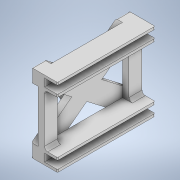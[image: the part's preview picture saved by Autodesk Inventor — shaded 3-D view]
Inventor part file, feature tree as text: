
AUTODESK INVENTOR PART (.ipt)
format: ipt  version: 2021 (Build 250183000, 183)  size: 252,928 bytes
history: native  units: in
note: dims shown in document units (in); Inventor stores cm internally (conversion verified against a paired STEP export)
features: extrude x4, fillet x4, sketch x4, plane x3
ambient origin geometry x8: Origin, YZ Plane, XZ Plane, XY Plane, X Axis, Y Axis, Z Axis, Center Point
bodies: Solid1 (feature_tree)
feature tree (15):
  extrude  "Extrusion1"  Depth=0.0394in TaperAngle=0.0deg
  plane  "Work Plane1"
  extrude  "Extrusion2"  Depth=0.5906in
  plane  "Work Plane2"
  extrude  "Extrusion3"  Depth=0.0787in
  plane  "Work Plane3"
  extrude  "Extrusion4"  Depth=0.0787in
  fillet  "Fillet1"  Radius=0.0787in
  fillet  "Fillet2"  Radius=0.0787in
  fillet  "Fillet3"  Radius=0.0787in
  fillet  "Fillet4"  Radius=0.0787in
  sketch  "Sketch1"  dims[d0=0.1969in d1=0.0394in d2=0.0in]
  sketch  "Sketch2"  dims[d3=0.0in d4=0.5906in]
  sketch  "Sketch3"  dims[d5=0.4724in d6=0.0787in]
  sketch  "Sketch4"  dims[d7=0.0787in d8=0.0787in d9=0.0787in d10=0.0787in d11=0.0787in d12=0.0787in d13=0.0787in d14=0.0394in d15=0.0in d16=0.0in d17=0.5906in d18=0.0394in d19=0.0in d20=0.0in d21=0.0157in d22=0.0157in d23=0.0157in d24=0.0157in d25=0.0787in d26=0.0in d27=0.0079in d28=0.0039in d29=0.0079in d30=0.0197in]
